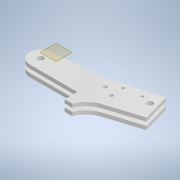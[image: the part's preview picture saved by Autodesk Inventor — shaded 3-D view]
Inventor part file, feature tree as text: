
AUTODESK INVENTOR PART (.ipt)
format: ipt  version: 2022 (Build 260153000, 153)  size: 297,472 bytes
history: native  units: mm
features: other x4, extrude x2, sketch x2
ambient origin geometry x8: Origin, YZ Plane, XZ Plane, XY Plane, X Axis, Y Axis, Z Axis, Center Point
bodies: Body1 (feature_tree)
feature tree (8):
  other  "Твердое тело1"
  other  "РабПлоскость3"
  other  "РабПлоскость4"
  extrude  "Выдавливание4"  Depth=5.0mm TaperAngle=0.0deg
  other  "РабПлоскость5"
  extrude  "Выдавливание5"  Depth=5.0mm TaperAngle=0.0deg
  sketch  "Эскиз4"
  sketch  "Эскиз5"
